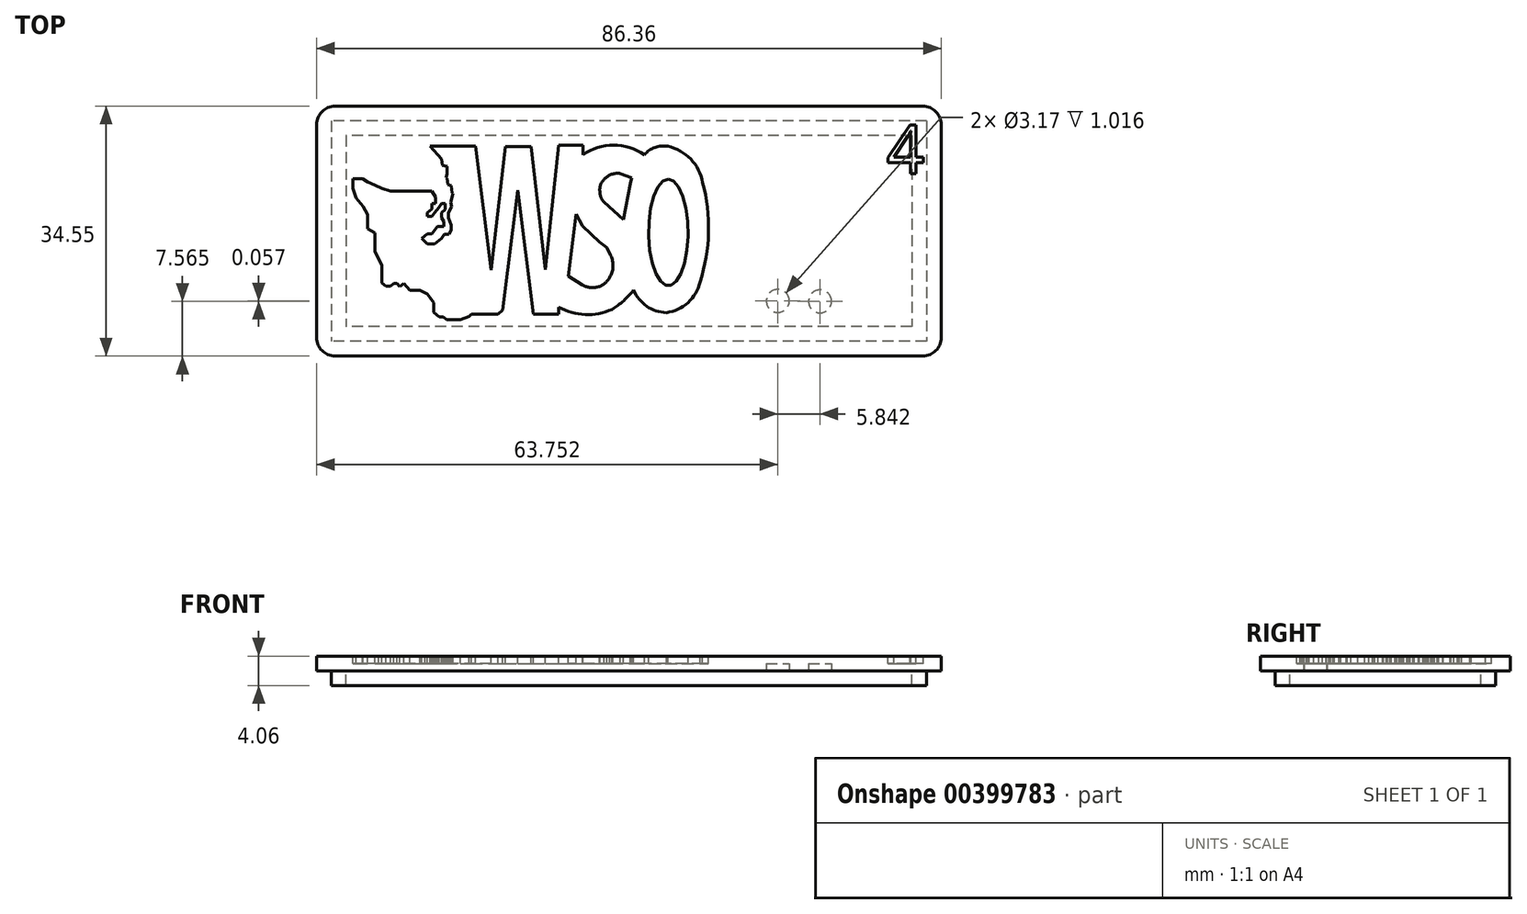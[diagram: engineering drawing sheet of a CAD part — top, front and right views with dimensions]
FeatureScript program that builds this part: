
annotation { "Feature Type Name" : "Feature", "Feature Type Description" : "" }
export const myFeature = defineFeature(function(context is Context, id is Id, definition is map)
    precondition{}
    {
        {
            var Q0;
            Q0=qCreatedBy(makeId("Top.planeOp"),FACE);
            var sketch = newSketch(context, id + "F0", { "sketchPlane" : qUnion([Q0])});
            skLineSegment(sketch, "E0.bottom", {"start": v(-37.27, 11.05) * mm, "end": v(49.09, 11.05) * mm});
            skLineSegment(sketch, "E0.top", {"start": v(-37.27, -23.5) * mm, "end": v(49.09, -23.5) * mm});
            skLineSegment(sketch, "E0.left", {"start": v(-37.27, 11.05) * mm, "end": v(-37.27, -23.5) * mm});
            skLineSegment(sketch, "E0.right", {"start": v(49.09, 11.05) * mm, "end": v(49.09, -23.5) * mm});
            skSolve(sketch);
        }
        {
            var Q0;
            Q0=makeQuery(id+"F0.imprint","IMPRINT",FACE,{"disambiguationData":[TD([[makeQuery(id+"F0.imprint","IMPRINT",EDGE,{"derivedFrom":sQuery(id+"F0.wireOp",EDGE,"E0.bottom")}),-1.0]])]});
            extrude(context, id + "F1", {"entities" : qUnion([Q0]), "depth" : 2.03 * mm});
        }
        {
            var Q0;
            Q0=makeQuery(id+"F1.opExtrude","SWEPT_EDGE",EDGE,{"disambiguationData":[OSD([sQuery(id+"F0.wireOp",EDGE,"E0.bottom"),sQuery(id+"F0.wireOp",EDGE,"E0.right")])]});
            var Q1;
            Q1=makeQuery(id+"F1.opExtrude","SWEPT_EDGE",EDGE,{"disambiguationData":[OSD([sQuery(id+"F0.wireOp",EDGE,"E0.top"),sQuery(id+"F0.wireOp",EDGE,"E0.right")])]});
            var Q2;
            Q2=makeQuery(id+"F1.opExtrude","SWEPT_EDGE",EDGE,{"disambiguationData":[OSD([sQuery(id+"F0.wireOp",EDGE,"E0.top"),sQuery(id+"F0.wireOp",EDGE,"E0.left")])]});
            var Q3;
            Q3=makeQuery(id+"F1.opExtrude","SWEPT_EDGE",EDGE,{"disambiguationData":[OSD([sQuery(id+"F0.wireOp",EDGE,"E0.bottom"),sQuery(id+"F0.wireOp",EDGE,"E0.left")])]});
            fillet(context, id + "F2", {"entities" : qUnion([Q0, Q1, Q2, Q3]), "radius" : 2.54 * mm, "tangentPropagation" : true, "allowEdgeOverflow" : false});
        }
        {
            var Q0;
            Q0=makeQuery(id+"F1.opExtrude","CAP_FACE",FACE,{"disambiguationData":[OSD([sQuery(id+"F0.wireOp",EDGE,"E0.bottom"),sQuery(id+"F0.wireOp",EDGE,"E0.top"),sQuery(id+"F0.wireOp",EDGE,"E0.left"),sQuery(id+"F0.wireOp",EDGE,"E0.right")])],"isStart":true});
            var sketch = newSketch(context, id + "F3", { "sketchPlane" : qUnion([Q0])});
            skLineSegment(sketch, "E1.bottom", {"start": v(47.06, -9.01) * mm, "end": v(-35.24, -9.01) * mm});
            skLineSegment(sketch, "E1.top", {"start": v(47.06, 21.47) * mm, "end": v(-35.24, 21.47) * mm});
            skLineSegment(sketch, "E1.left", {"start": v(47.06, -9.01) * mm, "end": v(47.06, 21.47) * mm});
            skLineSegment(sketch, "E1.right", {"start": v(-35.24, -9.01) * mm, "end": v(-35.24, 21.47) * mm});
            skLineSegment(sketch, "E2.0", {"start": v(45.02, -6.98) * mm, "end": v(-33.2, -6.98) * mm});
            skLineSegment(sketch, "E2.1", {"start": v(45.02, -6.98) * mm, "end": v(45.02, 19.43) * mm});
            skLineSegment(sketch, "E2.2", {"start": v(45.02, 19.43) * mm, "end": v(-33.2, 19.43) * mm});
            skLineSegment(sketch, "E2.3", {"start": v(-33.2, -6.98) * mm, "end": v(-33.2, 19.43) * mm});
            skSolve(sketch);
        }
        {
            var Q0;
            Q0=makeQuery(id+"F3.imprint","IMPRINT",FACE,{"disambiguationData":[TD([[makeQuery(id+"F3.imprint","IMPRINT",EDGE,{"derivedFrom":sQuery(id+"F3.wireOp",EDGE,"E1.bottom")}),-1.0]])]});
            extrude(context, id + "F4", {"entities" : qUnion([Q0]), "operationType" : NewBodyOperationType.ADD, "depth" : 2.03 * mm});
        }
        {
            var Q0;
            Q0=makeQuery(id+"F1.opExtrude","CAP_FACE",FACE,{"disambiguationData":[OSD([sQuery(id+"F0.wireOp",EDGE,"E0.bottom"),sQuery(id+"F0.wireOp",EDGE,"E0.top"),sQuery(id+"F0.wireOp",EDGE,"E0.left"),sQuery(id+"F0.wireOp",EDGE,"E0.right")])],"isStart":false});
            var sketch = newSketch(context, id + "F5", { "sketchPlane" : qUnion([Q0])});
            skCircle(sketch, "E3", {"center": v(26.48, -15.88) * mm, "radius": 1.59 * mm});
            skCircle(sketch, "E4.1.0.0", {"center": v(32.32, -15.94) * mm, "radius": 1.59 * mm});
            skLineSegment(sketch, "E4.direction1", {"start": v(26.48, -15.88) * mm, "end": v(32.32, -15.94) * mm, "construction": true});
            skSolve(sketch);
        }
        {
            var Q0;
            {var subQ0=sQuery(id+"F0.wireOp",EDGE,"E0.right");var subQ1=sQuery(id+"F0.wireOp",EDGE,"E0.left");var subQ2=sQuery(id+"F0.wireOp",EDGE,"E0.top");var subQ3=sQuery(id+"F0.wireOp",EDGE,"E0.bottom");var subQ4=makeQuery(id+"F1.opExtrude","CAP_FACE",FACE,{"disambiguationData":[OSD([subQ3,subQ2,subQ1,subQ0])],"isStart":true});Q0=makeQuery(id+"F8eOCUpTu3pMjdy_1.boolean.opBoolean","MERGE",FACE,{"derivedFrom":[makeQuery(id+"FJtGxXuQhMj2okl_1.boolean.opBoolean","MERGE",FACE,{"derivedFrom":[makeQuery(id+"F4.boolean.opBoolean","SPLIT",FACE,{"disambiguationData":[TD([makeQuery(id+"F1.opExtrude","SWEPT_FACE",FACE,{"disambiguationData":[OSD([subQ3])]})])],"derivedFrom":subQ4}),makeQuery(id+"F4.boolean.opBoolean","SPLIT",FACE,{"disambiguationData":[TD([makeQuery(id+"F4.opExtrude","SWEPT_FACE",FACE,{"disambiguationData":[OSD([sQuery(id+"F3.wireOp",EDGE,"E2.0")])]})])],"derivedFrom":subQ4}),makeQuery(id+"FJtGxXuQhMj2okl_1.opExtrude","CAP_FACE",FACE,{"disambiguationData":[OSD([sQuery(id+"FW5pSOtGTRrluGb_1.wireOp",EDGE,"BPr4tMOF-C45G-psBR-WNG2-PpbMrJUsswfe.bottom"),sQuery(id+"FW5pSOtGTRrluGb_1.wireOp",EDGE,"BPr4tMOF-C45G-psBR-WNG2-PpbMrJUsswfe.top"),sQuery(id+"FW5pSOtGTRrluGb_1.wireOp",EDGE,"BPr4tMOF-C45G-psBR-WNG2-PpbMrJUsswfe.left"),sQuery(id+"FW5pSOtGTRrluGb_1.wireOp",EDGE,"BPr4tMOF-C45G-psBR-WNG2-PpbMrJUsswfe.right")])],"isStart":false})]}),makeQuery(id+"F8eOCUpTu3pMjdy_1.opExtrude","CAP_FACE",FACE,{"disambiguationData":[OSD([sQuery(id+"FxFLyEuBG8TiyGk_1.wireOp",EDGE,"hmhw3Ft3-gyD9-b6cV-7Dsk-NiwxCSZjqCWs.bottom"),sQuery(id+"FxFLyEuBG8TiyGk_1.wireOp",EDGE,"hmhw3Ft3-gyD9-b6cV-7Dsk-NiwxCSZjqCWs.top"),sQuery(id+"FxFLyEuBG8TiyGk_1.wireOp",EDGE,"hmhw3Ft3-gyD9-b6cV-7Dsk-NiwxCSZjqCWs.left"),sQuery(id+"FxFLyEuBG8TiyGk_1.wireOp",EDGE,"hmhw3Ft3-gyD9-b6cV-7Dsk-NiwxCSZjqCWs.right")])],"isStart":false})]});}
            var sketch = newSketch(context, id + "F6", { "sketchPlane" : qUnion([Q0])});
            skCircle(sketch, "E5", {"center": v(26.48, 15.88) * mm, "radius": 1.59 * mm});
            skCircle(sketch, "E6", {"center": v(32.32, 15.94) * mm, "radius": 1.59 * mm});
            skSolve(sketch);
        }
        {
            var Q0;
            Q0 = qSketchRegion(id + "F6", true);
            extrude(context, id + "F7", {"entities" : qUnion([Q0]), "operationType" : NewBodyOperationType.REMOVE, "oppositeDirection" : true, "depth" : 1.02 * mm});
        }
        {
            var Q0;
            Q0=makeQuery(id+"F5.imprint","IMPRINT",FACE,{"disambiguationData":[TD([[makeQuery(id+"F5.imprint","IMPRINT",EDGE,{"derivedFrom":sQuery(id+"F5.wireOp",EDGE,"E3")}),-1.0]])]});
            var sketch = newSketch(context, id + "F8", { "sketchPlane" : qUnion([Q0])});
            skLineSegment(sketch, "E7", {"start": v(-21.32, -0.68) * mm, "end": v(-22.99, -0.68) * mm});
            skLineSegment(sketch, "E8", {"start": v(-22.99, -0.68) * mm, "end": v(-27.04, -0.68) * mm});
            skLineSegment(sketch, "E9", {"start": v(-27.04, -0.68) * mm, "end": v(-28.25, -0.28) * mm});
            skLineSegment(sketch, "E10", {"start": v(-28.25, -0.28) * mm, "end": v(-29.21, 0.13) * mm});
            skLineSegment(sketch, "E11", {"start": v(-29.21, 0.13) * mm, "end": v(-30.22, 0.58) * mm});
            skLineSegment(sketch, "E12", {"start": v(-30.22, 0.58) * mm, "end": v(-30.93, 1.04) * mm});
            skLineSegment(sketch, "E13", {"start": v(-30.93, 1.04) * mm, "end": v(-32.25, 1.04) * mm});
            skLineSegment(sketch, "E14", {"start": v(-32.25, 1.04) * mm, "end": v(-32.25, -0.28) * mm});
            skLineSegment(sketch, "E15", {"start": v(-32.25, -0.28) * mm, "end": v(-31.84, -1.64) * mm});
            skLineSegment(sketch, "E16", {"start": v(-31.84, -1.64) * mm, "end": v(-30.88, -2.8) * mm});
            skLineSegment(sketch, "E17", {"start": v(-30.88, -2.8) * mm, "end": v(-30.22, -3.92) * mm});
            skLineSegment(sketch, "E18", {"start": v(-30.22, -3.92) * mm, "end": v(-30.22, -5.9) * mm});
            skLineSegment(sketch, "E19", {"start": v(-30.22, -5.9) * mm, "end": v(-29.21, -6.45) * mm});
            skLineSegment(sketch, "E20", {"start": v(-29.21, -6.45) * mm, "end": v(-29.21, -9.08) * mm});
            skLineSegment(sketch, "E21", {"start": v(-29.21, -9.08) * mm, "end": v(-28.7, -10.04) * mm});
            skLineSegment(sketch, "E22", {"start": v(-28.7, -10.04) * mm, "end": v(-28.25, -10.95) * mm});
            skLineSegment(sketch, "E23", {"start": v(-28.25, -10.95) * mm, "end": v(-28.25, -13.38) * mm});
            skLineSegment(sketch, "E24", {"start": v(-28.25, -13.38) * mm, "end": v(-27.7, -13.84) * mm});
            skLineSegment(sketch, "E25", {"start": v(-27.7, -13.84) * mm, "end": v(-27.04, -13.84) * mm});
            skLineSegment(sketch, "E26", {"start": v(-27.04, -13.84) * mm, "end": v(-26.63, -13.43) * mm});
            skLineSegment(sketch, "E27", {"start": v(-26.63, -13.43) * mm, "end": v(-26.18, -13.43) * mm});
            skLineSegment(sketch, "E28", {"start": v(-26.18, -13.43) * mm, "end": v(-25.8, -13.91) * mm});
            skLineSegment(sketch, "E29", {"start": v(-25.8, -13.91) * mm, "end": v(-25.18, -13.43) * mm});
            skLineSegment(sketch, "E30", {"start": v(-25.18, -13.43) * mm, "end": v(-24.41, -14.43) * mm});
            skLineSegment(sketch, "E31", {"start": v(-24.41, -14.43) * mm, "end": v(-22.99, -14.43) * mm});
            skLineSegment(sketch, "E32", {"start": v(-22.99, -14.43) * mm, "end": v(-21.97, -14.9) * mm});
            skLineSegment(sketch, "E33", {"start": v(-21.97, -14.9) * mm, "end": v(-21.57, -15.45) * mm});
            skLineSegment(sketch, "E34", {"start": v(-21.57, -15.45) * mm, "end": v(-21.07, -16.12) * mm});
            skLineSegment(sketch, "E35", {"start": v(-21.07, -16.12) * mm, "end": v(-21.07, -17.43) * mm});
            skLineSegment(sketch, "E36", {"start": v(-21.07, -17.43) * mm, "end": v(-20.35, -18.06) * mm});
            skLineSegment(sketch, "E37", {"start": v(-20.35, -18.06) * mm, "end": v(-19.76, -18.06) * mm});
            skLineSegment(sketch, "E38", {"start": v(-19.76, -18.06) * mm, "end": v(-19.31, -18.47) * mm});
            skLineSegment(sketch, "E39", {"start": v(-19.31, -18.47) * mm, "end": v(-17.38, -18.47) * mm});
            skLineSegment(sketch, "E40", {"start": v(-17.38, -18.47) * mm, "end": v(-16.2, -18.02) * mm});
            skLineSegment(sketch, "E41", {"start": v(-16.2, -18.02) * mm, "end": v(-15.85, -17.7) * mm});
            skLineSegment(sketch, "E42", {"start": v(-15.85, -17.7) * mm, "end": v(-12.16, -17.7) * mm});
            skLineSegment(sketch, "E43", {"start": v(-12.16, -17.7) * mm, "end": v(-11.55, -17.13) * mm});
            skLineSegment(sketch, "E44", {"start": v(-11.55, -17.13) * mm, "end": v(-9.46, -0.54) * mm});
            skLineSegment(sketch, "E45", {"start": v(-9.46, -0.54) * mm, "end": v(-7.28, -17.7) * mm});
            skLineSegment(sketch, "E46", {"start": v(-7.28, -17.7) * mm, "end": v(-3.79, -17.7) * mm});
            skLineSegment(sketch, "E47", {"start": v(-3.79, -17.7) * mm, "end": v(-3.79, -16.74) * mm});
            skArc(sketch, "E48", {"start": v(3.57, -17.04) * mm, "mid": v(5.18, -15.84) * mm, "end": v(6.55, -14.37) * mm});
            skArc(sketch, "E49", {"start": v(6.55, -14.37) * mm, "mid": v(8.36, -16.6) * mm, "end": v(11.09, -17.5) * mm});
            skArc(sketch, "E50", {"start": v(11.09, -17.5) * mm, "mid": v(14.07, -16.1) * mm, "end": v(15.72, -13.25) * mm});
            skArc(sketch, "E51", {"start": v(15.72, -13.25) * mm, "mid": v(16.9, -6.4) * mm, "end": v(16.1, 0.5) * mm});
            skArc(sketch, "E52", {"start": v(16.1, 0.5) * mm, "mid": v(14.45, 3.74) * mm, "end": v(11.27, 5.5) * mm});
            skArc(sketch, "E53", {"start": v(11.27, 5.5) * mm, "mid": v(9.5, 5.35) * mm, "end": v(8.04, 4.32) * mm});
            skArc(sketch, "E54", {"start": v(8.04, 4.32) * mm, "mid": v(3.79, 5.66) * mm, "end": v(-0.47, 4.32) * mm});
            skLineSegment(sketch, "E55", {"start": v(-13.15, -11.63) * mm, "end": v(-11.17, 5.44) * mm});
            skLineSegment(sketch, "E56", {"start": v(-11.17, 5.44) * mm, "end": v(-7.61, 5.44) * mm});
            skLineSegment(sketch, "E57", {"start": v(-7.61, 5.44) * mm, "end": v(-5.63, -11.52) * mm});
            skLineSegment(sketch, "E58", {"start": v(-5.63, -11.52) * mm, "end": v(-3.8, 5.66) * mm});
            skPoint(sketch, "E58.endSnap0", {"position": v(3.79, 5.66) * mm});
            skLineSegment(sketch, "E59", {"start": v(-3.8, 5.66) * mm, "end": v(-0.47, 5.66) * mm});
            skLineSegment(sketch, "E60", {"start": v(-0.47, 5.66) * mm, "end": v(-0.47, 4.32) * mm});
            skEllipse(sketch, "E61", {"center": v(11.34, -6.4) * mm, "majorRadius": 7.36 * mm, "minorRadius": 2.73 * mm, "majorAxis": v(0, 1)});
            skPoint(sketch, "E61.centerSnap0", {"position": v(16.9, -6.4) * mm});
            skLineSegment(sketch, "E62", {"start": v(-1.4, -3.84) * mm, "end": v(-2.45, -12.41) * mm});
            skLineSegment(sketch, "E63", {"start": v(-2.45, -12.41) * mm, "end": v(-0.56, -13.62) * mm});
            skArc(sketch, "E64", {"start": v(-0.56, -13.62) * mm, "mid": v(1.55, -13.96) * mm, "end": v(3.23, -12.64) * mm});
            skLineSegment(sketch, "E65", {"start": v(-1.4, -3.84) * mm, "end": v(-0.48, -5.51) * mm});
            skLineSegment(sketch, "E66", {"start": v(-0.48, -5.51) * mm, "end": v(1.87, -7.71) * mm});
            skLineSegment(sketch, "E67", {"start": v(1.87, -7.71) * mm, "end": v(2.85, -8.53) * mm});
            skLineSegment(sketch, "E68", {"start": v(2.85, -8.53) * mm, "end": v(3.38, -9.6) * mm});
            skArc(sketch, "E69", {"start": v(3.23, -12.64) * mm, "mid": v(3.7, -11.14) * mm, "end": v(3.38, -9.6) * mm});
            skLineSegment(sketch, "E70", {"start": v(6.29, 1.13) * mm, "end": v(6.1, 0.31) * mm});
            skLineSegment(sketch, "E71", {"start": v(6.1, 0.31) * mm, "end": v(5.14, -4.64) * mm});
            skLineSegment(sketch, "E72", {"start": v(5.14, -4.64) * mm, "end": v(2.5, -2.24) * mm});
            skArc(sketch, "E73", {"start": v(1.91, -0.97) * mm, "mid": v(2.08, -1.66) * mm, "end": v(2.5, -2.24) * mm});
            skArc(sketch, "E74", {"start": v(2.5, 0.95) * mm, "mid": v(1.96, 0.06) * mm, "end": v(1.91, -0.97) * mm});
            skArc(sketch, "E75", {"start": v(4.72, 1.74) * mm, "mid": v(3.5, 1.63) * mm, "end": v(2.5, 0.95) * mm});
            skLineSegment(sketch, "E76", {"start": v(6.29, 1.13) * mm, "end": v(4.72, 1.74) * mm});
            skLineSegment(sketch, "E77", {"start": v(-13.15, -11.63) * mm, "end": v(-15.33, 5.56) * mm});
            skLineSegment(sketch, "E78", {"start": v(-15.33, 5.56) * mm, "end": v(-21.6, 5.56) * mm});
            skLineSegment(sketch, "E79", {"start": v(-21.6, 5.56) * mm, "end": v(-19.98, 3.78) * mm});
            skLineSegment(sketch, "E80", {"start": v(-19.98, 3.78) * mm, "end": v(-19.86, 2.86) * mm});
            skLineSegment(sketch, "E81", {"start": v(-19.86, 2.86) * mm, "end": v(-19.26, 2.72) * mm});
            skLineSegment(sketch, "E82", {"start": v(-19.26, 2.72) * mm, "end": v(-19.26, 1.74) * mm});
            skLineSegment(sketch, "E83", {"start": v(-19.26, 1.74) * mm, "end": v(-19.4, 1.13) * mm});
            skLineSegment(sketch, "E84", {"start": v(-19.4, 1.13) * mm, "end": v(-19.26, 1.1) * mm});
            skLineSegment(sketch, "E85", {"start": v(-19.26, 1.1) * mm, "end": v(-19.14, 0.18) * mm});
            skLineSegment(sketch, "E86", {"start": v(-19.14, 0.18) * mm, "end": v(-18.7, 0.07) * mm});
            skLineSegment(sketch, "E87", {"start": v(-18.7, 0.07) * mm, "end": v(-18.56, -0.97) * mm});
            skLineSegment(sketch, "E88", {"start": v(-18.56, -0.97) * mm, "end": v(-18.44, -1) * mm});
            skLineSegment(sketch, "E89", {"start": v(-18.44, -1) * mm, "end": v(-18.72, -2.2) * mm});
            skLineSegment(sketch, "E90", {"start": v(-18.72, -2.2) * mm, "end": v(-18.63, -2.88) * mm});
            skLineSegment(sketch, "E91", {"start": v(-21.32, -0.68) * mm, "end": v(-20.84, -1.52) * mm});
            skLineSegment(sketch, "E92", {"start": v(-20.84, -1.52) * mm, "end": v(-20.84, -2.43) * mm});
            skLineSegment(sketch, "E93", {"start": v(-20.84, -2.43) * mm, "end": v(-21.32, -2.43) * mm});
            skLineSegment(sketch, "E94", {"start": v(-21.32, -2.43) * mm, "end": v(-21.32, -3.2) * mm});
            skLineSegment(sketch, "E95", {"start": v(-21.32, -3.2) * mm, "end": v(-21.99, -3.67) * mm});
            skLineSegment(sketch, "E96", {"start": v(-21.99, -3.67) * mm, "end": v(-21.99, -4.15) * mm});
            skLineSegment(sketch, "E97", {"start": v(-21.99, -4.15) * mm, "end": v(-21.32, -4.15) * mm});
            skLineSegment(sketch, "E98", {"start": v(-21.32, -4.15) * mm, "end": v(-20.98, -3.67) * mm});
            skLineSegment(sketch, "E99", {"start": v(-20.98, -3.67) * mm, "end": v(-20.41, -2.96) * mm});
            skLineSegment(sketch, "E100", {"start": v(-20.41, -2.96) * mm, "end": v(-19.98, -2.38) * mm});
            skLineSegment(sketch, "E101", {"start": v(-19.98, -2.38) * mm, "end": v(-19.5, -2.38) * mm});
            skLineSegment(sketch, "E102", {"start": v(-19.5, -2.38) * mm, "end": v(-19.5, -3.24) * mm});
            skLineSegment(sketch, "E103", {"start": v(-19.5, -3.24) * mm, "end": v(-20.03, -3.67) * mm});
            skLineSegment(sketch, "E104", {"start": v(-20.03, -3.67) * mm, "end": v(-20.03, -4.34) * mm});
            skLineSegment(sketch, "E105", {"start": v(-20.03, -4.34) * mm, "end": v(-19.7, -4.87) * mm});
            skLineSegment(sketch, "E106", {"start": v(-19.7, -4.87) * mm, "end": v(-19.7, -5.58) * mm});
            skLineSegment(sketch, "E107", {"start": v(-19.7, -5.58) * mm, "end": v(-20.55, -5.58) * mm});
            skLineSegment(sketch, "E108", {"start": v(-20.55, -5.58) * mm, "end": v(-21.32, -6.59) * mm});
            skLineSegment(sketch, "E109", {"start": v(-21.32, -6.59) * mm, "end": v(-21.99, -6.59) * mm});
            skLineSegment(sketch, "E110", {"start": v(-21.99, -6.59) * mm, "end": v(-22.7, -7.2) * mm});
            skLineSegment(sketch, "E111", {"start": v(-22.7, -7.2) * mm, "end": v(-22.31, -7.66) * mm});
            skLineSegment(sketch, "E112", {"start": v(-22.31, -7.66) * mm, "end": v(-21.99, -8.02) * mm});
            skLineSegment(sketch, "E113", {"start": v(-21.99, -8.02) * mm, "end": v(-20.98, -8.02) * mm});
            skLineSegment(sketch, "E114", {"start": v(-20.98, -8.02) * mm, "end": v(-20.03, -7.25) * mm});
            skLineSegment(sketch, "E115", {"start": v(-20.03, -7.25) * mm, "end": v(-19.65, -6.63) * mm});
            skLineSegment(sketch, "E116", {"start": v(-19.65, -6.63) * mm, "end": v(-18.98, -6.63) * mm});
            skLineSegment(sketch, "E117", {"start": v(-18.98, -6.63) * mm, "end": v(-18.64, -6.1) * mm});
            skLineSegment(sketch, "E118", {"start": v(-18.64, -6.1) * mm, "end": v(-18.64, -5.4) * mm});
            skLineSegment(sketch, "E119", {"start": v(-18.64, -5.4) * mm, "end": v(-19.07, -4.34) * mm});
            skLineSegment(sketch, "E120", {"start": v(-19.07, -4.34) * mm, "end": v(-19.07, -3.67) * mm});
            skLineSegment(sketch, "E121", {"start": v(-19.07, -3.67) * mm, "end": v(-18.63, -2.88) * mm});
            skPoint(sketch, "E122.end.orphan", {"position": v(-1.72, -17.7) * mm});
            skArc(sketch, "E123", {"start": v(-3.79, -16.74) * mm, "mid": v(-0.14, -17.76) * mm, "end": v(3.57, -17.04) * mm});
            skSolve(sketch);
        }
        {
            var Q0;
            Q0 = qSketchRegion(id + "F8", true);
            extrude(context, id + "F9", {"entities" : qUnion([Q0]), "operationType" : NewBodyOperationType.REMOVE, "oppositeDirection" : true, "depth" : 1.02 * mm, "offsetDistance" : 25.4 * mm});
        }
        {
            var Q0;
            Q0=makeQuery(id+"F5.imprint","IMPRINT",FACE,{"disambiguationData":[TD([[makeQuery(id+"F5.imprint","IMPRINT",EDGE,{"derivedFrom":sQuery(id+"F5.wireOp",EDGE,"E3")}),-1.0]])]});
            var sketch = newSketch(context, id + "F10", { "sketchPlane" : qUnion([Q0])});
            skText(sketch, "E124", { "text": "4", "fontName": "DroidSansMono.ttf"});
            const initialGuessF10  = {"E124": [0.04143, 0.00174, 1, 0, 0.00676]};
            skSetInitialGuess(sketch, initialGuessF10);
            skSolve(sketch);
        }
        {
            var Q0;
            Q0 = qSketchRegion(id + "F10", true);
            extrude(context, id + "F11", {"entities" : qUnion([Q0]), "operationType" : NewBodyOperationType.REMOVE, "oppositeDirection" : true, "depth" : 1.02 * mm, "offsetDistance" : 25.4 * mm});
        }
    });
